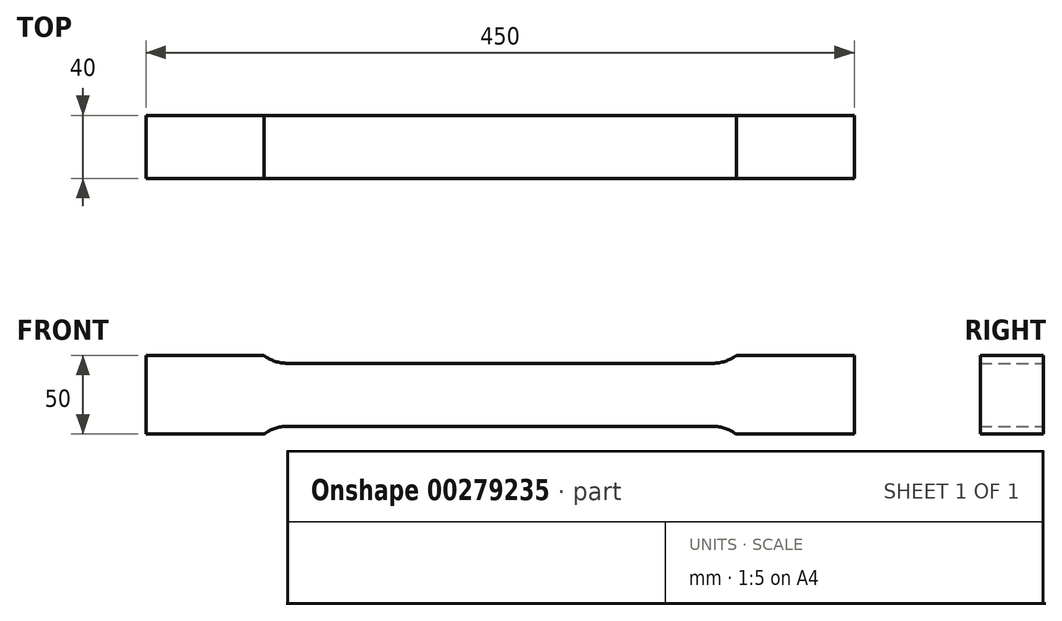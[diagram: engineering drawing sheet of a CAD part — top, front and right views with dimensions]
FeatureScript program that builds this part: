
annotation { "Feature Type Name" : "Feature", "Feature Type Description" : "" }
export const myFeature = defineFeature(function(context is Context, id is Id, definition is map)
    precondition{}
    {
        {
            var Q0;
            Q0=qCreatedBy(makeId("Front.planeOp"),FACE);
            var sketch = newSketch(context, id + "F0", { "sketchPlane" : qUnion([Q0])});
            skLineSegment(sketch, "E0", {"start": v(0, 20) * mm, "end": v(135, 20) * mm});
            skArc(sketch, "E1", {"start": v(135, 20) * mm, "mid": v(142.9, 21.28) * mm, "end": v(150, 25) * mm});
            skLineSegment(sketch, "E2", {"start": v(150, 25) * mm, "end": v(225, 25) * mm});
            skLineSegment(sketch, "E3", {"start": v(225, 25) * mm, "end": v(225, 0) * mm});
            skLineSegment(sketch, "E4.MirrorCS", {"start": v(0, -20) * mm, "end": v(135, -20) * mm});
            skLineSegment(sketch, "E5.MirrorCS", {"start": v(225, -25) * mm, "end": v(225, 0) * mm});
            skLineSegment(sketch, "E6.MirrorCS", {"start": v(150, -25) * mm, "end": v(225, -25) * mm});
            skArc(sketch, "E7.MirrorCS", {"start": v(135, -20) * mm, "mid": v(142.9, -21.28) * mm, "end": v(150, -25) * mm});
            skArc(sketch, "E8.MirrorCS", {"start": v(-135, -20) * mm, "mid": v(-142.9, -21.28) * mm, "end": v(-150, -25) * mm});
            skArc(sketch, "E9.MirrorCS", {"start": v(-135, 20) * mm, "mid": v(-142.9, 21.28) * mm, "end": v(-150, 25) * mm});
            skLineSegment(sketch, "E10.MirrorCS", {"start": v(-150, -25) * mm, "end": v(-225, -25) * mm});
            skLineSegment(sketch, "E11.MirrorCS", {"start": v(-150, 25) * mm, "end": v(-225, 25) * mm});
            skLineSegment(sketch, "E12.MirrorCS", {"start": v(-225, -25) * mm, "end": v(-225, 0) * mm});
            skLineSegment(sketch, "E13.MirrorCS", {"start": v(0, -20) * mm, "end": v(-135, -20) * mm});
            skLineSegment(sketch, "E14.MirrorCS", {"start": v(-225, 25) * mm, "end": v(-225, 0) * mm});
            skLineSegment(sketch, "E15.MirrorCS", {"start": v(0, 20) * mm, "end": v(-135, 20) * mm});
            skSolve(sketch);
        }
        {
            var Q0;
            Q0 = qSketchRegion(id + "F0", true);
            extrude(context, id + "F1", {"entities" : qUnion([Q0]), "endBound" : BoundingType.SYMMETRIC, "depth" : 40 * mm});
        }
    });
